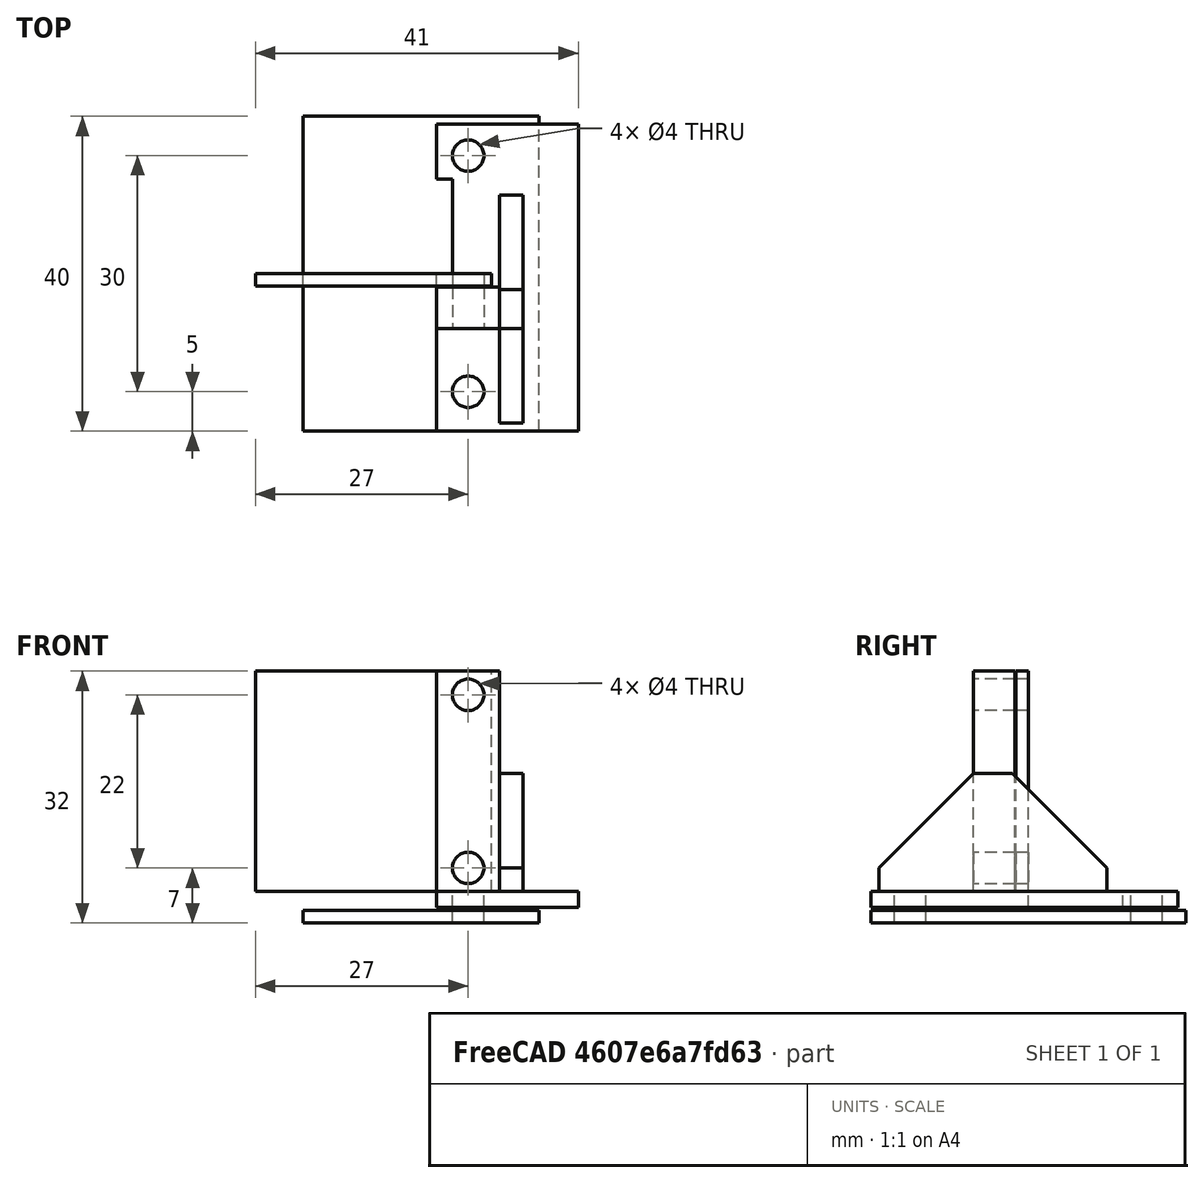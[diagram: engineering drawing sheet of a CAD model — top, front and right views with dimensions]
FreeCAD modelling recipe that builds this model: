
FCSTD DOCUMENT  (FreeCAD 0.19R24291 (Git))
Label: holder_com
License: All rights reserved
LicenseURL: http://en.wikipedia.org/wiki/All_rights_reserved
objects: Part::Cylinder×8, Part::Box×6, Part::MultiFuse×4, Part::Cut×3, Part::Chamfer×1
note: 22 computed .brp shape members not serialized (recipe doc carries the construction recipe); baked Part::Feature solids carry a one-line shape summary decoded from their .brp

FEATURE [Part::Box] Box  label="Cube"
  AttacherType = Attacher::AttachEngine3D
  Height = 1.6
  Length = 30
  Width = 40
FEATURE [Part::Box] Box001  label="Cube001"
  AttacherType = Attacher::AttachEngine3D
  Height = 1.6
  Length = 30
  Width = 28
FEATURE [Part::Cylinder] Cylinder
  Angle = 360
  AttacherType = Attacher::AttachEngine3D
  Height = 10
  Placement = pos=(21,5,0) rot=(0,0,1;0rad)
  Radius = 2
FEATURE [Part::Cylinder] Cylinder001
  Angle = 360
  AttacherType = Attacher::AttachEngine3D
  Height = 10
  Placement = pos=(21,35,0) rot=(0,0,1;0rad)
  Radius = 2
FEATURE [Part::MultiFuse] Fusion
  Shapes = -> [Cylinder001,Cylinder]
FEATURE [Part::Cut] Cut  label="back_panel"
  Base = -> Box
  Tool = -> Fusion
FEATURE [Part::Cylinder] Cylinder002
  Angle = 360
  AttacherType = Attacher::AttachEngine3D
  Height = 10
  Placement = pos=(27,3,0) rot=(0,0,1;0rad)
  Radius = 2
FEATURE [Part::Cylinder] Cylinder003
  Angle = 360
  AttacherType = Attacher::AttachEngine3D
  Height = 10
  Placement = pos=(27,25,0) rot=(0,0,1;0rad)
  Radius = 2
FEATURE [Part::MultiFuse] Fusion001
  Shapes = -> [Cylinder002,Cylinder003]
FEATURE [Part::Cut] Cut001  label="PCB"
  Base = -> Box001
  Placement = pos=(-6,20,4) rot=(1,0,0;1.5708rad)
  Tool = -> Fusion001
FEATURE [Part::Box] Box002  label="Cube002"
  AttacherType = Attacher::AttachEngine3D
  Height = 2
  Length = 18
  Placement = pos=(17,0,2) rot=(0,0,1;0rad)
  Width = 39
FEATURE [Part::Box] Box003  label="Cube003"
  AttacherType = Attacher::AttachEngine3D
  Height = 30
  Length = 8
  Placement = pos=(17,13,2) rot=(0,0,1;0rad)
  Width = 5.3
FEATURE [Part::Box] Box004  label="Cube004"
  AttacherType = Attacher::AttachEngine3D
  Height = 17
  Length = 3
  Placement = pos=(25,1,2) rot=(0,0,1;0rad)
  Width = 29
FEATURE [Part::Cylinder] Cylinder004
  Angle = 360
  AttacherType = Attacher::AttachEngine3D
  Height = 10
  Placement = pos=(21,5,0) rot=(0,0,1;0rad)
  Radius = 2
FEATURE [Part::Cylinder] Cylinder005
  Angle = 360
  AttacherType = Attacher::AttachEngine3D
  Height = 10
  Placement = pos=(21,35,0) rot=(0,0,1;0rad)
  Radius = 2
FEATURE [Part::Cylinder] Cylinder006
  Angle = 360
  AttacherType = Attacher::AttachEngine3D
  Height = 13
  Placement = pos=(21,22,29) rot=(1,0,0;1.5708rad)
  Radius = 2
FEATURE [Part::Cylinder] Cylinder007
  Angle = 360
  AttacherType = Attacher::AttachEngine3D
  Height = 12
  Placement = pos=(21,21,7) rot=(1,0,0;1.5708rad)
  Radius = 2
FEATURE [Part::Chamfer] Chamfer
  Base = -> Box004
  Edges = 2 edges r=12: [Edge10,Edge12]
FEATURE [Part::Box] Box005  label="Cube005"
  AttacherType = Attacher::AttachEngine3D
  Height = 2
  Length = 2
  Placement = pos=(17,20,2) rot=(0,0,1;0rad)
  Width = 12
FEATURE [Part::MultiFuse] Fusion002
  Shapes = -> [Cylinder004,Cylinder005,Cylinder006,Cylinder007,Box005]
FEATURE [Part::MultiFuse] Fusion003
  Shapes = -> [Box002,Box003,Chamfer]
FEATURE [Part::Cut] Cut002  label="holder"
  Base = -> Fusion003
  Tool = -> Fusion002
